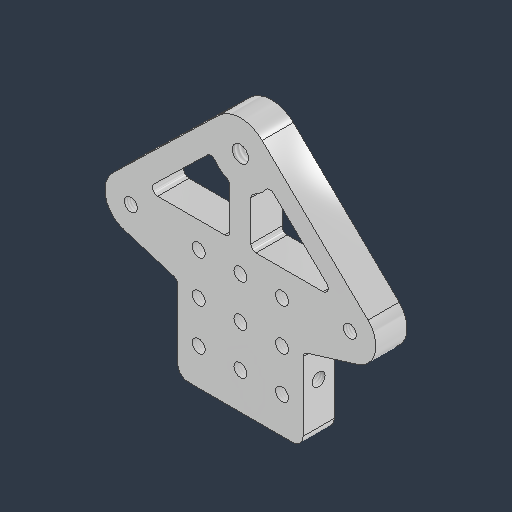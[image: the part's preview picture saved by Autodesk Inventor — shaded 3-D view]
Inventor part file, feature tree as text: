
AUTODESK INVENTOR PART (.ipt)
format: ipt  version: 2024.3 (Build 283343000, 343)  size: 299,520 bytes
history: native  units: in
note: dims shown in document units (in); Inventor stores cm internally (conversion verified against a paired STEP export)
features: sketch x5, hole x4, fillet x2, extrude x1, projected_geometry x1
ambient origin geometry x8: Origin, YZ Plane, XZ Plane, XY Plane, X Axis, Y Axis, Z Axis, Center Point
bodies: Body1 (feature_tree)
feature tree (13):
  extrude  "Extrusion2"  Depth=0.3125in
  hole  "Hole1"  [1 undecoded]
  hole  "Hole2"  [1 undecoded]
  hole  "Hole3"  [1 undecoded]
  hole  "Hole4"  [1 undecoded]
  fillet  "Fillet5"  Radius=0.875in
  fillet  "Fillet7"  Radius=0.0625in
  sketch  "Sketch1"  dims[d24=2.005in d25=0.3125in]
  sketch  "Sketch2"  dims[d26=1.0in d30=0.25in]
  sketch  "Sketch3"  dims[d32=0.375in d33=0.0in]
  sketch  "Sketch6"  dims[d34=0.156in d35=0.38in d36=0.375in d37=0.25in d38=0.5635in d39=1.0in d40=0.8108in d43=1.0in]
  projected_geometry  "Projected Loop1"
  sketch  "Sketch7"  dims[d45=0.0625in d46=0.156in d47=0.38in d48=0.375in d49=0.19in d50=0.5635in d51=0.536in d52=0.8108in d64=0.125in d65=0.156in d66=0.38in d67=0.375in d68=0.25in d69=0.5635in d70=1.0in d71=0.8108in d73=0.5in d74=0.875in d95=0.196in d96=0.5in d97=0.375in d98=0.25in d99=0.5635in d100=1.0in d101=0.8108in d103=0.0625in d105=1.1811in d107=0.5in d108=0.3937in d110=1.0in d112=0.375in d113=1.1875in d115=0.25in d116=0.25in d117=0.25in]
note: 4 required parameter values undecoded (feature->parameter linkage not recoverable at this tier; creation-order binding heuristic only, values carry confidence <= 0.55)
